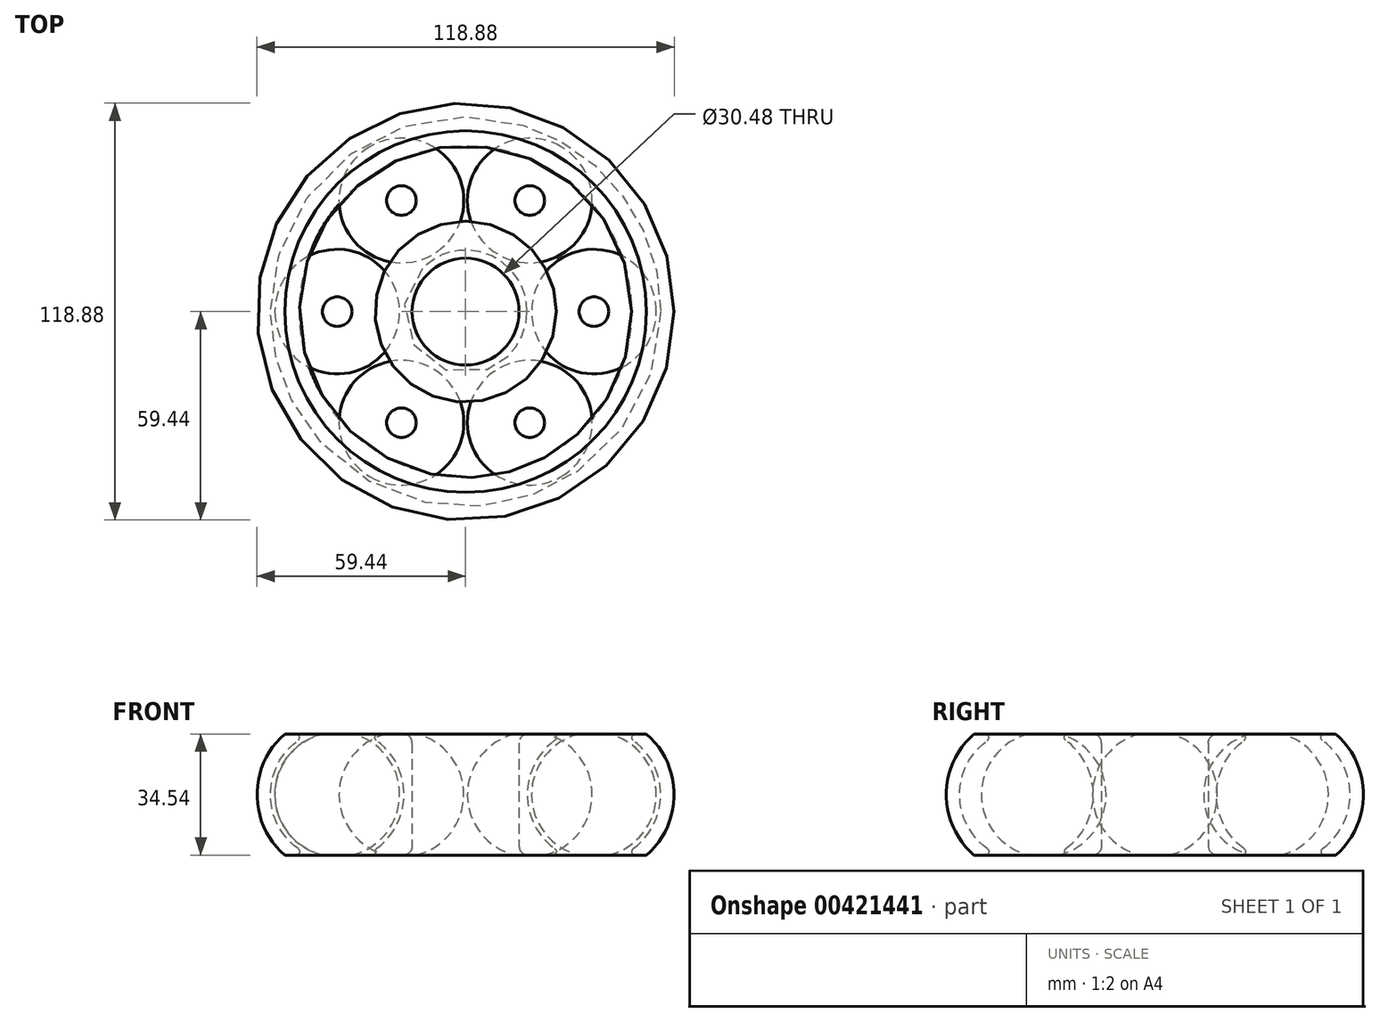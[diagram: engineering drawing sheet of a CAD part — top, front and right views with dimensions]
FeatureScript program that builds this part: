
annotation { "Feature Type Name" : "Feature", "Feature Type Description" : "" }
export const myFeature = defineFeature(function(context is Context, id is Id, definition is map)
    precondition{}
    {
        {
            var Q0;
            Q0=qCreatedBy(makeId("Front.planeOp"),FACE);
            var sketch = newSketch(context, id + "F0", { "sketchPlane" : qUnion([Q0])});
            skLineSegment(sketch, "E0.1.0.0", {"start": v(21.6, -17.27) * mm, "end": v(28.54, -17.27) * mm});
            skLineSegment(sketch, "E0.1.0.1", {"start": v(21.6, 17.27) * mm, "end": v(28.54, 17.27) * mm});
            skArc(sketch, "E0.1.0.2", {"start": v(40.8, -17.27) * mm, "mid": v(54.36, 0) * mm, "end": v(40.8, 17.27) * mm});
            skArc(sketch, "E0.1.0.3", {"start": v(32.36, 17.27) * mm, "mid": v(18.8, 0) * mm, "end": v(32.36, -17.27) * mm});
            skArc(sketch, "E0.1.0.4", {"start": v(44.61, -17.27) * mm, "mid": v(55.63, 0) * mm, "end": v(44.61, 17.27) * mm});
            skArc(sketch, "E0.1.0.5", {"start": v(28.54, 17.27) * mm, "mid": v(17.53, 0) * mm, "end": v(28.54, -17.27) * mm});
            skLineSegment(sketch, "E0.1.0.6", {"start": v(32.36, 17.27) * mm, "end": v(40.8, 17.27) * mm});
            skLineSegment(sketch, "E0.1.0.8", {"start": v(44.61, 17.27) * mm, "end": v(51.55, 17.27) * mm});
            skLineSegment(sketch, "E0.1.0.9", {"start": v(44.61, -17.27) * mm, "end": v(51.55, -17.27) * mm});
            skLineSegment(sketch, "E0.1.0.10", {"start": v(32.36, -17.27) * mm, "end": v(40.8, -17.27) * mm});
            skArc(sketch, "E0.1.0.11", {"start": v(21.6, 17.27) * mm, "mid": v(13.72, 0) * mm, "end": v(21.6, -17.27) * mm});
            skArc(sketch, "E0.1.0.12", {"start": v(51.55, -17.27) * mm, "mid": v(59.44, 0) * mm, "end": v(51.55, 17.27) * mm});
            skLineSegment(sketch, "E1", {"start": v(0, 0) * mm, "end": v(36.58, 0) * mm, "construction": true});
            skSolve(sketch);
        }
        {
            var Q0;
            Q0=qCreatedBy(makeId("Front.planeOp"),FACE);
            var sketch = newSketch(context, id + "F1", { "sketchPlane" : qUnion([Q0])});
            skLineSegment(sketch, "E2", {"start": v(0, 0) * mm, "end": v(0, -7.86) * mm, "construction": true});
            skSolve(sketch);
        }
        {
            var Q0;
            Q0=makeQuery(id+"F0.imprint","IMPRINT",FACE,{"disambiguationData":[TD([[makeQuery(id+"F0.imprint","IMPRINT",EDGE,{"derivedFrom":sQuery(id+"F0.wireOp",EDGE,"aMwJVjsy-r012-ixN0-n996-qMEVEzDtUZkf")}),-1.0]])]});
            var Q1;
            Q1=makeQuery(id+"F0.imprint","IMPRINT",FACE,{"disambiguationData":[TD([[makeQuery(id+"F0.imprint","IMPRINT",EDGE,{"derivedFrom":sQuery(id+"F0.wireOp",EDGE,"E0.1.0.0")}),1.0]])]});
            var Q2;
            Q2=sQuery(id+"F1.wireOp",EDGE,"E2");
            revolve(context, id + "F2", {"entities" : qUnion([Q0, Q1]), "axis" : qUnion([Q2]), "revolveType" : RevolveType.FULL});
        }
        {
            var Q0;
            Q0=makeQuery(id+"F0.imprint","IMPRINT",FACE,{"disambiguationData":[TD([[makeQuery(id+"F0.imprint","IMPRINT",EDGE,{"derivedFrom":sQuery(id+"F0.wireOp",EDGE,"f678e9ec-c04d-4fb7-bd81-1e2353813811.trimOffspring")}),-1.0]])]});
            var Q1;
            Q1=makeQuery(id+"F0.imprint","IMPRINT",FACE,{"disambiguationData":[TD([[makeQuery(id+"F0.imprint","IMPRINT",EDGE,{"derivedFrom":sQuery(id+"F0.wireOp",EDGE,"E0.1.0.4")}),-1.0]])]});
            var Q2;
            Q2=sQuery(id+"F1.wireOp",EDGE,"E2");
            revolve(context, id + "F3", {"entities" : qUnion([Q0, Q1]), "axis" : qUnion([Q2]), "revolveType" : RevolveType.FULL});
        }
        {
            var Q0;
            Q0=qCreatedBy(makeId("Front.planeOp"),FACE);
            var sketch = newSketch(context, id + "F4", { "sketchPlane" : qUnion([Q0])});
            skLineSegment(sketch, "E3.0.0", {"start": v(36.58, 17.27) * mm, "end": v(32.36, 17.27) * mm});
            skArc(sketch, "E3.0.1", {"start": v(32.36, 17.27) * mm, "mid": v(18.8, 0) * mm, "end": v(32.36, -17.27) * mm});
            skLineSegment(sketch, "E3.0.2", {"start": v(32.36, -17.27) * mm, "end": v(36.58, -17.27) * mm});
            skLineSegment(sketch, "E4", {"start": v(36.58, 17.27) * mm, "end": v(36.58, -17.27) * mm});
            skPoint(sketch, "E3.0.3.end.orphan", {"position": v(40.8, 17.27) * mm});
            skPoint(sketch, "E5.orphan", {"position": v(40.8, -17.27) * mm});
            skSolve(sketch);
        }
        {
            var Q0;
            Q0=makeQuery(id+"F4.imprint","IMPRINT",FACE,{"disambiguationData":[TD([[makeQuery(id+"F4.imprint","IMPRINT",EDGE,{"derivedFrom":sQuery(id+"F4.wireOp",EDGE,"E3.0.0")}),1.0]])]});
            var Q1;
            Q1=sQuery(id+"F4.wireOp",EDGE,"E4");
            revolve(context, id + "F5", {"entities" : qUnion([Q0]), "axis" : qUnion([Q1]), "revolveType" : RevolveType.FULL});
        }
        {
            var Q0;
            Q0=makeQuery(id+"F5.opRevolve","SWEPT_BODY",BODY,{"disambiguationData":[OSD([sQuery(id+"F4.wireOp",EDGE,"E3.0.0"),sQuery(id+"F4.wireOp",EDGE,"E3.0.1"),sQuery(id+"F4.wireOp",EDGE,"E3.0.2"),sQuery(id+"F4.wireOp",EDGE,"E4")])]});
            var Q1;
            Q1=sQuery(id+"F1.wireOp",EDGE,"E2");
            circularPattern(context, id + "F6", {"entities" : qUnion([Q0]), "axis" : qUnion([Q1]), "angle" : 360 * degree, "instanceCount" : 6, "equalSpace" : true});
        }
        {
            var Q0;
            Q0=makeQuery(id+"F3.opRevolve","SWEPT_EDGE",EDGE,{"disambiguationData":[OSD([sQuery(id+"F0.wireOp",EDGE,"E0.1.0.4"),sQuery(id+"F0.wireOp",EDGE,"E0.1.0.8")])]});
            var Q1;
            Q1=makeQuery(id+"F2.opRevolve","SWEPT_EDGE",EDGE,{"disambiguationData":[OSD([sQuery(id+"F0.wireOp",EDGE,"E0.1.0.1"),sQuery(id+"F0.wireOp",EDGE,"E0.1.0.5")])]});
            var Q2;
            Q2=makeQuery(id+"F2.opRevolve","SWEPT_EDGE",EDGE,{"disambiguationData":[OSD([sQuery(id+"F0.wireOp",EDGE,"E0.1.0.0"),sQuery(id+"F0.wireOp",EDGE,"E0.1.0.5")])]});
            var Q3;
            Q3=makeQuery(id+"F3.opRevolve","SWEPT_EDGE",EDGE,{"disambiguationData":[OSD([sQuery(id+"F0.wireOp",EDGE,"E0.1.0.4"),sQuery(id+"F0.wireOp",EDGE,"E0.1.0.9")])]});
            fillet(context, id + "F7", {"entities" : qUnion([Q0, Q1, Q2, Q3]), "radius" : 1.02 * mm, "tangentPropagation" : true, "allowEdgeOverflow" : false});
        }
        {
            var Q0;
            Q0=makeQuery(id+"F2.opRevolve","SWEPT_FACE",FACE,{"disambiguationData":[OSD([sQuery(id+"F0.wireOp",EDGE,"E0.1.0.0")])]});
            var sketch = newSketch(context, id + "F8", { "sketchPlane" : qUnion([Q0])});
            skCircle(sketch, "E6", {"center": v(0, 0) * mm, "radius": 15.24 * mm});
            skCircle(sketch, "E7.0", {"center": v(0, 0) * mm, "radius": 21.6 * mm});
            skSolve(sketch);
        }
        {
            var Q0;
            Q0=makeQuery(id+"F8.imprint","IMPRINT",FACE,{"disambiguationData":[TD([[makeQuery(id+"F8.imprint","IMPRINT",EDGE,{"derivedFrom":sQuery(id+"F8.wireOp",EDGE,"E6")}),-1.0]])]});
            extrude(context, id + "F9", {"entities" : qUnion([Q0]), "endBound" : BoundingType.UP_TO_NEXT, "oppositeDirection" : true, "depth" : 25.4 * mm});
        }
        {
            var Q0;
            Q0=makeQuery(id+"F9.opExtrude","SWEPT_BODY",BODY,{"disambiguationData":[OSD([sQuery(id+"F8.wireOp",EDGE,"E6"),sQuery(id+"F8.wireOp",EDGE,"E7.0")])]});
            var Q1;
            Q1=qCreatedBy(makeId("Top.planeOp"),FACE);
            mirror(context, id + "F10", {"operationType" : NewBodyOperationType.ADD, "entities" : qUnion([Q0]), "mirrorPlane" : qUnion([Q1])});
        }
        {
            var Q0;
            Q0=makeQuery(id+"F9.opExtrude","CAP_EDGE",EDGE,{"disambiguationData":[OSD([sQuery(id+"F8.wireOp",EDGE,"E6")])],"isStart":true});
            var Q1;
            Q1=makeQuery(id+"F10.opPattern","COPY",EDGE,{"derivedFrom":makeQuery(id+"F9.opExtrude","CAP_EDGE",EDGE,{"disambiguationData":[OSD([sQuery(id+"F8.wireOp",EDGE,"E6")])],"isStart":true}),"instanceName":"1"});
            fillet(context, id + "F11", {"entities" : qUnion([Q0, Q1]), "radius" : 2.54 * mm, "tangentPropagation" : true, "allowEdgeOverflow" : false});
        }
        {
            var Q0;
            Q0=makeQuery(id+"F10.boolean.opBoolean","MERGE",FACE,{"derivedFrom":[makeQuery(id+"F2.opRevolve","SWEPT_FACE",FACE,{"disambiguationData":[OSD([sQuery(id+"F0.wireOp",EDGE,"E0.1.0.0")])]}),makeQuery(id+"F9.opExtrude","CAP_FACE",FACE,{"disambiguationData":[OSD([sQuery(id+"F8.wireOp",EDGE,"E6"),sQuery(id+"F8.wireOp",EDGE,"E7.0")])],"isStart":true})]});
            var sketch = newSketch(context, id + "F12", { "sketchPlane" : qUnion([Q0])});
            skCircle(sketch, "E8.0", {"center": v(0, 0) * mm, "radius": 15.24 * mm});
            skSolve(sketch);
        }
        {
            var Q0;
            Q0 = qSketchRegion(id + "F12", true);
            extrude(context, id + "F13", {"entities" : qUnion([Q0]), "operationType" : NewBodyOperationType.REMOVE, "oppositeDirection" : true, "depth" : 38.35 * mm});
        }
    });
